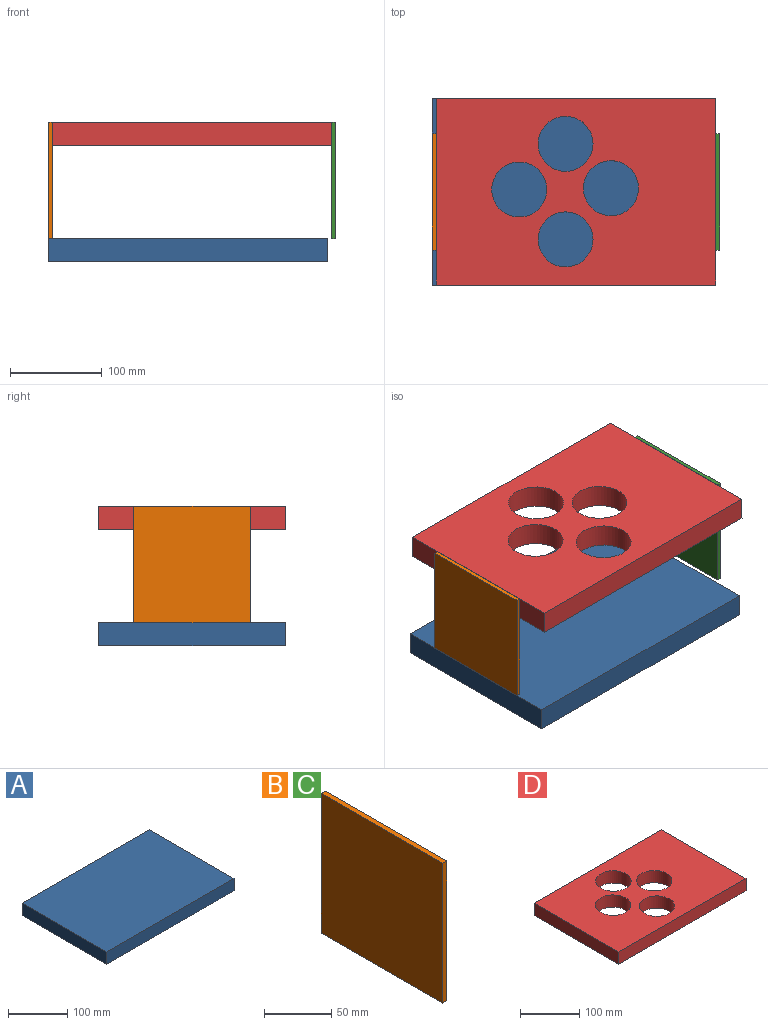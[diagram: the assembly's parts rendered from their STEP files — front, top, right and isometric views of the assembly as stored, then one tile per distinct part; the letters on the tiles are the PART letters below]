
ASSEMBLY  parts=4 mates=3
PART A: 6 faces, bbox 304.8x203.2x25.4 mm
  f0: plane 304.8x25.4mm, normal (0,1,0), area 7741.9mm2, adj f1,f3,f4,f5
  f1: plane 203.2x25.4mm, normal (-1,0,0), area 5161.3mm2, adj f0,f2,f4,f5
  f2: plane 304.8x25.4mm, normal (0,-1,0), area 7741.9mm2, adj f1,f3,f4,f5
  f3: plane 203.2x25.4mm, normal (1,0,0), area 5161.3mm2, adj f0,f2,f4,f5
  f4: plane 304.8x203.2mm, normal (0,0,1), area 61935.4mm2, adj f0,f1,f2,f3
  f5: plane 304.8x203.2mm, normal (0,0,-1), area 61935.4mm2, adj f0,f1,f2,f3
PART B: 6 faces, bbox 4.2x127x127 mm
  f0: plane 127x4.23mm, normal (0,0,1), area 537.6mm2, adj f1,f3,f4,f5
  f1: plane 127x4.23mm, normal (0,-1,0), area 537.6mm2, adj f0,f2,f4,f5
  f2: plane 127x4.23mm, normal (0,0,-1), area 537.6mm2, adj f1,f3,f4,f5
  f3: plane 127x4.23mm, normal (0,1,0), area 537.6mm2, adj f0,f2,f4,f5
  f4: plane 127x127mm, normal (1,0,0), area 16129mm2, adj f0,f1,f2,f3
  f5: plane 127x127mm, normal (-1,0,0), area 16129mm2, adj f0,f1,f2,f3
PART C: same geometry as B
PART D: 10 faces, bbox 304.8x203.2x25.4 mm
  f0: plane 304.8x25.4mm, normal (0,1,0), area 7741.9mm2, adj f1,f7,f8,f9
  f1: plane 203.2x25.4mm, normal (-1,0,0), area 5161.3mm2, adj f0,f2,f8,f9
  f2: plane 304.8x25.4mm, normal (0,-1,0), area 7741.9mm2, adj f1,f7,f8,f9
  f3: cylinder r=30mm len=60mm, axis (0,0,-1), area 4787.4mm2, adj f8,f9
  f4: cylinder r=30mm len=59.99mm, axis (0,0,-1), area 4787.4mm2, adj f8,f9
  f5: cylinder r=30mm len=60mm, axis (0,0,-1), area 4787.8mm2, adj f8,f9
  f6: cylinder r=30mm len=60mm, axis (0,0,-1), area 4787.4mm2, adj f8,f9
  f7: plane 203.2x25.4mm, normal (1,0,0), area 5161.3mm2, adj f0,f2,f8,f9
  f8: plane 304.8x203.2mm, normal (0,0,1), area 50627.1mm2, adj f0,f1,f2,f3,f4,f5,f6,f7
  f9: plane 304.8x203.2mm, normal (0,0,-1), area 50627.1mm2, adj f0,f1,f2,f3,f4,f5,f6,f7
PLACE A t=(-16.96,-89.46,-88.4)mm
PLACE B t=(-148.75,-78.69,31.15)mm
PLACE C t=(160.29,-78.69,31.15)mm
PLACE D t=(-3.52,-120.36,38.6)mm
MATE fastened B.f4 <-> D.f1  axis (1,0,0) through (-144.51,-78.55,64)mm
MATE fastened A.f4 <-> B.f2  axis (0,0,1) through (-148.75,-78.55,-63)mm
MATE fastened C.f5 <-> D.f7  axis (-1,0,0) through (160.29,-78.55,64)mm
